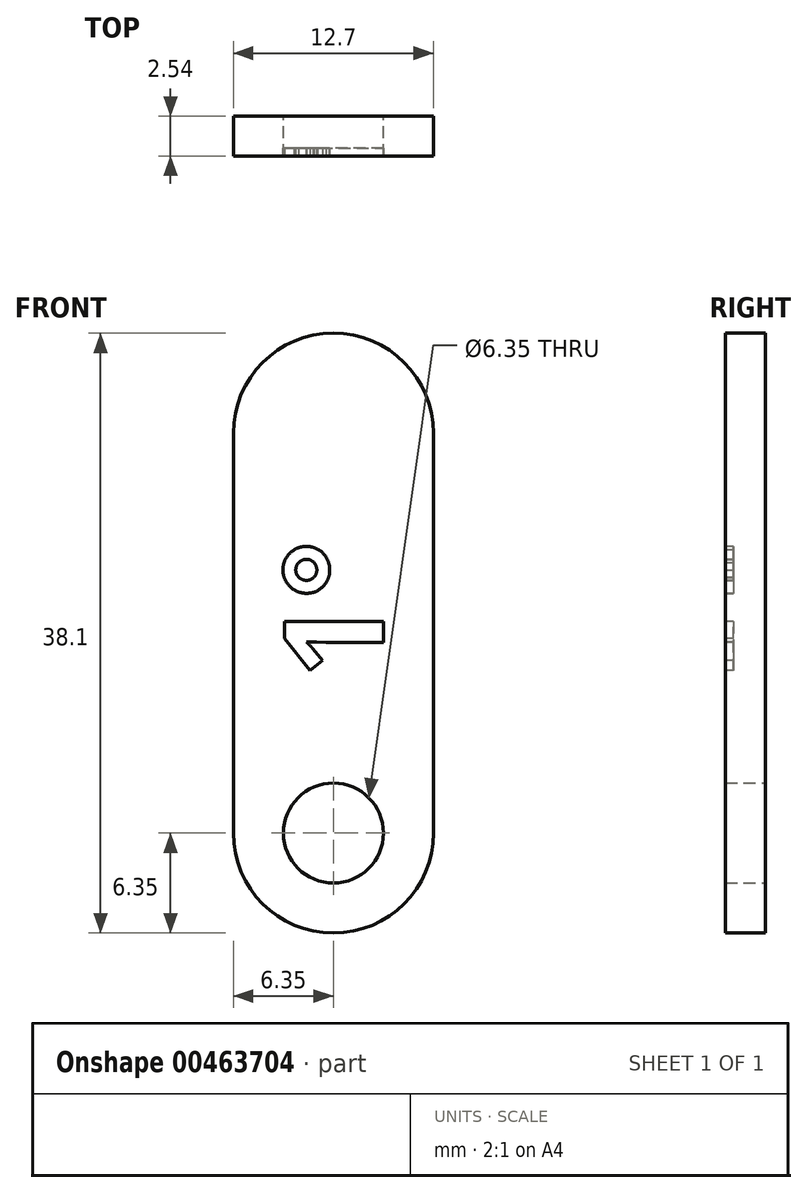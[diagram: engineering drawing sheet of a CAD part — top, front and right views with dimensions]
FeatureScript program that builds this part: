
annotation { "Feature Type Name" : "Feature", "Feature Type Description" : "" }
export const myFeature = defineFeature(function(context is Context, id is Id, definition is map)
    precondition{}
    {
        {
            var Q0;
            Q0=qCreatedBy(makeId("Front.planeOp"),FACE);
            var sketch = newSketch(context, id + "F0", { "sketchPlane" : qUnion([Q0])});
            skLineSegment(sketch, "E0.bottom", {"start": v(0, 0) * mm, "end": v(12.7, 0) * mm});
            skLineSegment(sketch, "E0.top", {"start": v(0, 38.1) * mm, "end": v(12.7, 38.1) * mm});
            skLineSegment(sketch, "E0.left", {"start": v(0, 0) * mm, "end": v(0, 38.1) * mm});
            skLineSegment(sketch, "E0.right", {"start": v(12.7, 0) * mm, "end": v(12.7, 38.1) * mm});
            skCircle(sketch, "E1", {"center": v(6.35, 6.35) * mm, "radius": 3.18 * mm});
            skSolve(sketch);
        }
        {
            var Q0;
            Q0=makeQuery(id+"F0.imprint","IMPRINT",FACE,{"disambiguationData":[TD([[makeQuery(id+"F0.imprint","IMPRINT",EDGE,{"derivedFrom":sQuery(id+"F0.wireOp",EDGE,"E0.bottom")}),1.0]])]});
            extrude(context, id + "F1", {"entities" : qUnion([Q0]), "depth" : 2.54 * mm});
        }
        {
            var Q0;
            Q0=makeQuery(id+"F1.opExtrude","SWEPT_EDGE",EDGE,{"disambiguationData":[OSD([sQuery(id+"F0.wireOp",EDGE,"E0.bottom"),sQuery(id+"F0.wireOp",EDGE,"E0.right")])]});
            var Q1;
            Q1=makeQuery(id+"F1.opExtrude","SWEPT_EDGE",EDGE,{"disambiguationData":[OSD([sQuery(id+"F0.wireOp",EDGE,"E0.bottom"),sQuery(id+"F0.wireOp",EDGE,"E0.left")])]});
            var Q2;
            Q2=makeQuery(id+"F1.opExtrude","SWEPT_EDGE",EDGE,{"disambiguationData":[OSD([sQuery(id+"F0.wireOp",EDGE,"E0.top"),sQuery(id+"F0.wireOp",EDGE,"E0.right")])]});
            var Q3;
            Q3=makeQuery(id+"F1.opExtrude","SWEPT_EDGE",EDGE,{"disambiguationData":[OSD([sQuery(id+"F0.wireOp",EDGE,"E0.top"),sQuery(id+"F0.wireOp",EDGE,"E0.left")])]});
            fillet(context, id + "F2", {"entities" : qUnion([Q0, Q1, Q2, Q3]), "radius" : 6.35 * mm, "tangentPropagation" : true, "allowEdgeOverflow" : false});
        }
        {
            var Q0;
            Q0=makeQuery(id+"F1.opExtrude","CAP_FACE",FACE,{"disambiguationData":[OSD([sQuery(id+"F0.wireOp",EDGE,"E0.bottom"),sQuery(id+"F0.wireOp",EDGE,"E0.top"),sQuery(id+"F0.wireOp",EDGE,"E0.left"),sQuery(id+"F0.wireOp",EDGE,"E0.right"),sQuery(id+"F0.wireOp",EDGE,"E1")])],"isStart":false});
            var sketch = newSketch(context, id + "F3", { "sketchPlane" : qUnion([Q0])});
            skText(sketch, "E2", { "text": "1°", "fontName": "OpenSans-Bold.ttf"});
            skLineSegment(sketch, "E3", {"start": v(0, 31.75) * mm, "end": v(12.7, 31.75) * mm, "construction": true});
            skLineSegment(sketch, "E4", {"start": v(6.35, 31.75) * mm, "end": v(6.35, 9.53) * mm, "construction": true});
            skPoint(sketch, "E4.endSnap0", {"position": v(6.35, 20.64) * mm});
            const initialGuessF3  = {"E2": [0.00953, 0.01615, 0, 1, 0.00635]};
            skSetInitialGuess(sketch, initialGuessF3);
            skSolve(sketch);
        }
        {
            var Q0;
            Q0=qSketchRegion(id+"F3",true);
            extrude(context, id + "F4", {"entities" : qUnion([Q0]), "operationType" : NewBodyOperationType.REMOVE, "oppositeDirection" : true, "depth" : 0.5 * mm});
        }
    });
